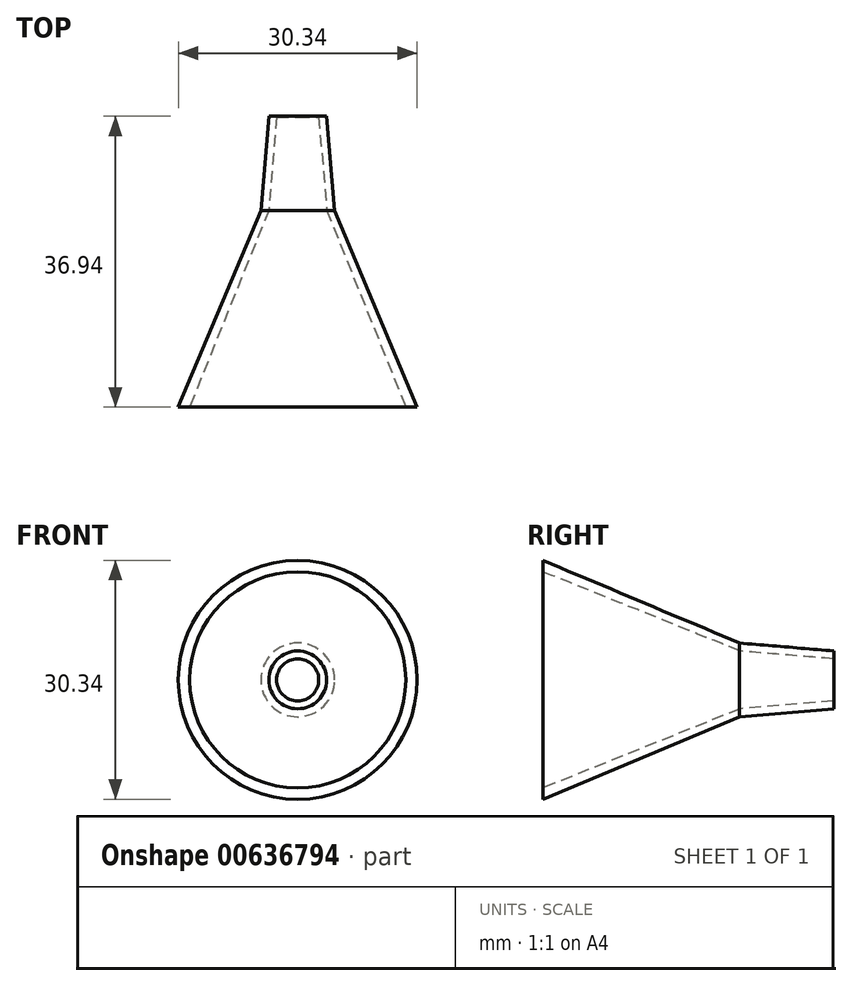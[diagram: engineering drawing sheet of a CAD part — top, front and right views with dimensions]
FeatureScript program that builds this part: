
annotation { "Feature Type Name" : "Feature", "Feature Type Description" : "" }
export const myFeature = defineFeature(function(context is Context, id is Id, definition is map)
    precondition{}
    {
        {
            var Q0;
            Q0=qCreatedBy(makeId("Right.planeOp"),FACE);
            var sketch = newSketch(context, id + "F0", { "sketchPlane" : qUnion([Q0])});
            skLineSegment(sketch, "E0", {"start": v(-0.14, -2.5) * mm, "end": v(-12, -3.5) * mm});
            skLineSegment(sketch, "E1", {"start": v(-0.14, -2.5) * mm, "end": v(-0.06, -3.5) * mm});
            skLineSegment(sketch, "E2", {"start": v(-0.06, -3.5) * mm, "end": v(-12.06, -4.51) * mm});
            skLineSegment(sketch, "E3", {"start": v(-12.06, -4.51) * mm, "end": v(-37, -15) * mm});
            skLineSegment(sketch, "E4", {"start": v(-37, -15) * mm, "end": v(-37, -13.56) * mm});
            skLineSegment(sketch, "E5", {"start": v(-37, -13.56) * mm, "end": v(-12, -3.5) * mm});
            skLineSegment(sketch, "E6", {"start": v(12.35, 0.17) * mm, "end": v(-62.75, 0.17) * mm, "construction": true});
            skSolve(sketch);
        }
        {
            var Q0;
            Q0=makeQuery(id+"F0.imprint","IMPRINT",FACE,{"disambiguationData":[TD([[makeQuery(id+"F0.imprint","IMPRINT",EDGE,{"derivedFrom":sQuery(id+"F0.wireOp",EDGE,"E0")}),1.0]])]});
            var Q1;
            Q1=sQuery(id+"F0.wireOp",EDGE,"E6");
            revolve(context, id + "F1", {"entities" : qUnion([Q0]), "axis" : qUnion([Q1]), "revolveType" : RevolveType.FULL});
        }
    });
